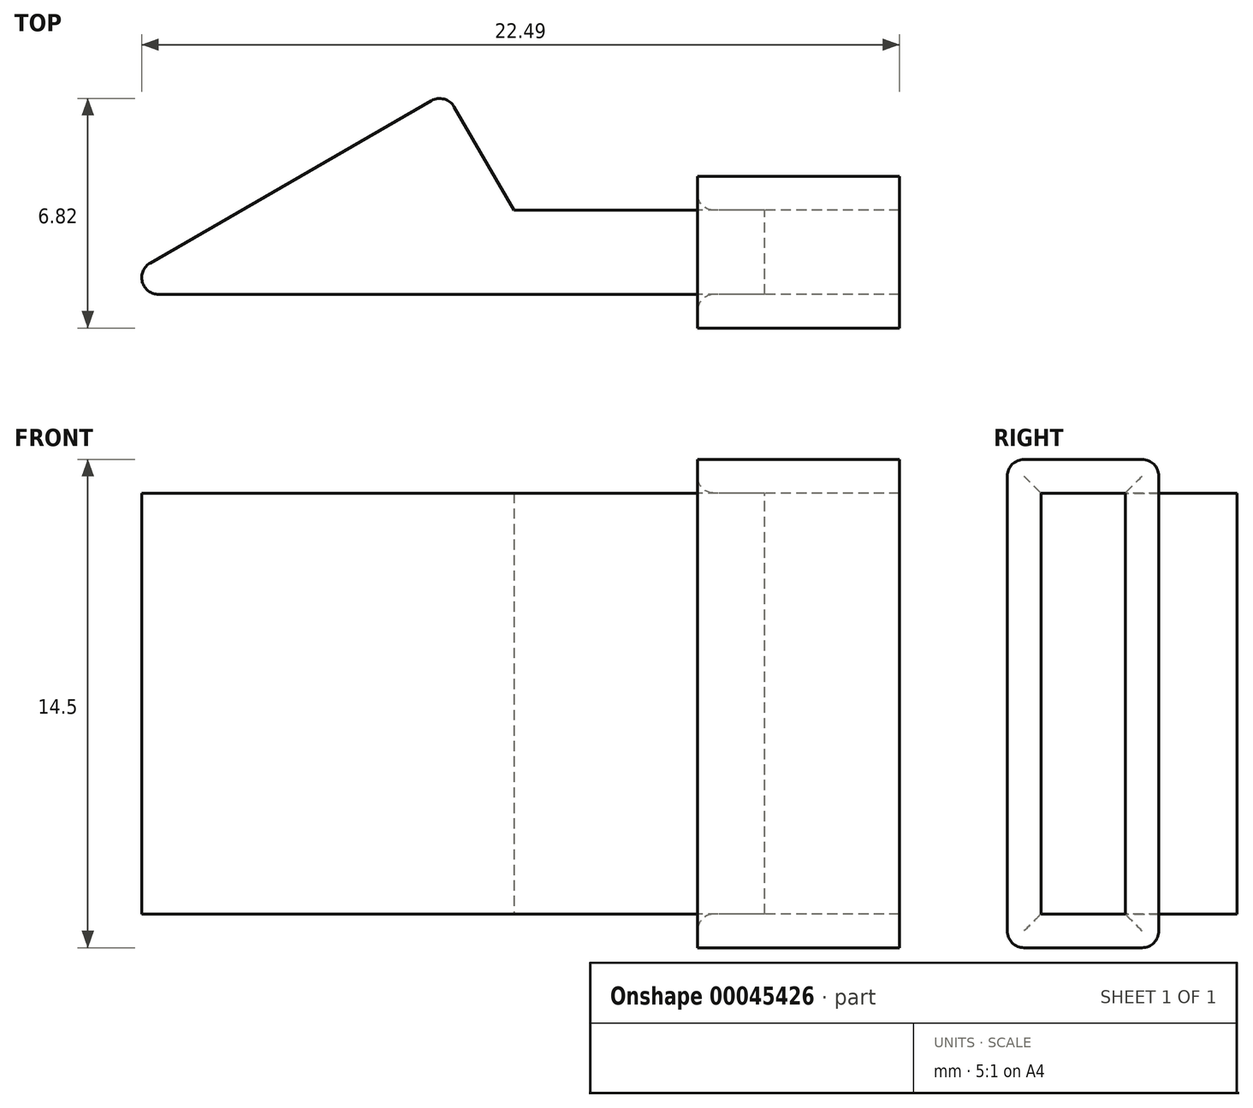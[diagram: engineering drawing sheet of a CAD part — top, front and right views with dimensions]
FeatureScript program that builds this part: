
annotation { "Feature Type Name" : "Feature", "Feature Type Description" : "" }
export const myFeature = defineFeature(function(context is Context, id is Id, definition is map)
    precondition{}
    {
        {
            var Q0;
            Q0=qCreatedBy(makeId("Top.planeOp"),FACE);
            var sketch = newSketch(context, id + "F0", { "sketchPlane" : qUnion([Q0])});
            skLineSegment(sketch, "E0", {"start": v(0, 0) * mm, "end": v(-13.86, 0) * mm});
            skLineSegment(sketch, "E1", {"start": v(-13.86, 0) * mm, "end": v(-3.46, 6) * mm});
            skLineSegment(sketch, "E2", {"start": v(-3.46, 6) * mm, "end": v(0, 0) * mm});
            skLineSegment(sketch, "E3", {"start": v(-3.46, 6) * mm, "end": v(-3.46, 0) * mm, "construction": true});
            skSolve(sketch);
        }
        {
            var Q0;
            Q0=qSketchRegion(id+"F0",true);
            extrude(context, id + "F1", {"entities" : qUnion([Q0]), "depth" : 12.5 * mm});
        }
        {
            var Q0;
            Q0=qCreatedBy(makeId("Right.planeOp"),FACE);
            cPlane(context, id + "F2", {"entities" : qUnion([Q0]), "cplaneType" : CPlaneType.OFFSET, "offset" : 3.46 * mm, "oppositeDirection" : true, "width" : 150 * mm, "height" : 150 * mm});
        }
        {
            var Q0;
            Q0=qCreatedBy(id+"F2.planeOp",FACE);
            var sketch = newSketch(context, id + "F3", { "sketchPlane" : qUnion([Q0])});
            skLineSegment(sketch, "E4.bottom", {"start": v(0, 0) * mm, "end": v(2.5, 0) * mm});
            skLineSegment(sketch, "E4.top", {"start": v(0, 12.5) * mm, "end": v(2.5, 12.5) * mm});
            skLineSegment(sketch, "E4.left", {"start": v(0, 0) * mm, "end": v(0, 12.5) * mm});
            skLineSegment(sketch, "E4.right", {"start": v(2.5, 0) * mm, "end": v(2.5, 12.5) * mm});
            skSolve(sketch);
        }
        {
            var Q0;
            Q0=qSketchRegion(id+"F3",true);
            extrude(context, id + "F4", {"entities" : qUnion([Q0]), "operationType" : NewBodyOperationType.ADD, "depth" : 9.46 * mm});
        }
        {
            var Q0;
            Q0=makeQuery(id+"F4.opExtrude","CAP_FACE",FACE,{"disambiguationData":[OSD([sQuery(id+"F3.wireOp",EDGE,"E4.bottom"),sQuery(id+"F3.wireOp",EDGE,"E4.top"),sQuery(id+"F3.wireOp",EDGE,"E4.left"),sQuery(id+"F3.wireOp",EDGE,"E4.right")])],"isStart":false});
            var sketch = newSketch(context, id + "F5", { "sketchPlane" : qUnion([Q0])});
            skLineSegment(sketch, "E5.bottom", {"start": v(0, 12.5) * mm, "end": v(2.5, 12.5) * mm});
            skLineSegment(sketch, "E5.top", {"start": v(0, 0) * mm, "end": v(2.5, 0) * mm});
            skLineSegment(sketch, "E5.left", {"start": v(0, 12.5) * mm, "end": v(0, 0) * mm});
            skLineSegment(sketch, "E5.right", {"start": v(2.5, 12.5) * mm, "end": v(2.5, 0) * mm});
            skLineSegment(sketch, "E6.bottom", {"start": v(-1, 13.5) * mm, "end": v(3.5, 13.5) * mm});
            skLineSegment(sketch, "E6.top", {"start": v(-1, -1) * mm, "end": v(3.5, -1) * mm});
            skLineSegment(sketch, "E6.left", {"start": v(-1, 13.5) * mm, "end": v(-1, -1) * mm});
            skLineSegment(sketch, "E6.right", {"start": v(3.5, 13.5) * mm, "end": v(3.5, -1) * mm});
            skSolve(sketch);
        }
        {
            var Q0;
            Q0=makeQuery(id+"F5.imprint","IMPRINT",FACE,{"disambiguationData":[TD([[makeQuery(id+"F5.imprint","IMPRINT",EDGE,{"derivedFrom":sQuery(id+"F5.wireOp",EDGE,"E5.bottom")}),1.0]])]});
            extrude(context, id + "F6", {"entities" : qUnion([Q0]), "depth" : 4 * mm, "hasSecondDirection" : true, "secondDirectionOppositeDirection" : true, "secondDirectionDepth" : 2 * mm});
        }
        {
            var Q0;
            Q0=makeQuery(id+"F1.opExtrude","SWEPT_EDGE",EDGE,{"disambiguationData":[OSD([sQuery(id+"F0.wireOp",EDGE,"E0"),sQuery(id+"F0.wireOp",EDGE,"E1")])]});
            var Q1;
            Q1=makeQuery(id+"F1.opExtrude","SWEPT_EDGE",EDGE,{"disambiguationData":[OSD([sQuery(id+"F0.wireOp",EDGE,"E1"),sQuery(id+"F0.wireOp",EDGE,"E2")])]});
            fillet(context, id + "F7", {"entities" : qUnion([Q0, Q1]), "radius" : .5 * mm, "tangentPropagation" : true, "allowEdgeOverflow" : false});
        }
        {
            var Q0;
            Q0=makeQuery(id+"F6.opExtrude","CAP_EDGE",EDGE,{"disambiguationData":[OSD([sQuery(id+"F5.wireOp",EDGE,"E5.top")])],"isStart":true});
            var Q1;
            Q1=makeQuery(id+"F6.opExtrude","CAP_EDGE",EDGE,{"disambiguationData":[OSD([sQuery(id+"F5.wireOp",EDGE,"E5.left")])],"isStart":true});
            var Q2;
            Q2=makeQuery(id+"F6.opExtrude","CAP_EDGE",EDGE,{"disambiguationData":[OSD([sQuery(id+"F5.wireOp",EDGE,"E5.right")])],"isStart":true});
            var Q3;
            Q3=makeQuery(id+"F6.opExtrude","CAP_EDGE",EDGE,{"disambiguationData":[OSD([sQuery(id+"F5.wireOp",EDGE,"E5.bottom")])],"isStart":true});
            var Q4;
            Q4=makeQuery(id+"F6.opExtrude","SWEPT_EDGE",EDGE,{"disambiguationData":[OSD([sQuery(id+"F5.wireOp",EDGE,"E6.bottom"),sQuery(id+"F5.wireOp",EDGE,"E6.left")])]});
            var Q5;
            Q5=makeQuery(id+"F6.opExtrude","SWEPT_EDGE",EDGE,{"disambiguationData":[OSD([sQuery(id+"F5.wireOp",EDGE,"E6.bottom"),sQuery(id+"F5.wireOp",EDGE,"E6.right")])]});
            var Q6;
            Q6=makeQuery(id+"F6.opExtrude","SWEPT_EDGE",EDGE,{"disambiguationData":[OSD([sQuery(id+"F5.wireOp",EDGE,"E6.top"),sQuery(id+"F5.wireOp",EDGE,"E6.right")])]});
            var Q7;
            Q7=makeQuery(id+"F6.opExtrude","SWEPT_EDGE",EDGE,{"disambiguationData":[OSD([sQuery(id+"F5.wireOp",EDGE,"E6.top"),sQuery(id+"F5.wireOp",EDGE,"E6.left")])]});
            fillet(context, id + "F8", {"entities" : qUnion([Q0, Q1, Q2, Q3, Q4, Q5, Q6, Q7]), "radius" : .5 * mm, "tangentPropagation" : true, "allowEdgeOverflow" : false});
        }
    });
